# Revit family: PRD_FrankeWS_TwlRls_MEDIUSDoubleTowelRack_MEDX012HP
name_source: partatom
category: Specialty Equipment
revit_build: Autodesk Revit 2018 (Build: 20190510_1515(x64)
units: mm (PartAtom-declared; Revit-internal decimal feet)

## family parameters
Cut with Voids When Loaded = No
Host = Face
OmniClass Number = 23.40.20.21.27
OmniClass Title = Towel Bars
Part Type = Normal
Room Calculation Point = No
Round Connector Dimension = Use Diameter
Shared = No

## types (1)
- MEDX012HP
    AssetType = Fixed
    BIMObjectName = PRD_AR_TowelRails_MEDIUSDoubleTowelRack_MEDX012HP
    Category = Pr_40_20_76_90, Towel rails
    Default Elevation = 1200 mm
    Description = Double towel rack in combination of towel shelf and rail for wall mounting, 304 stainless steel, round covers to conceal the fixing of screws, inclusive stainless steel screws and dowels.
    DurationUnit = year
    Features = stainless steel, surface high polished
    Finish = high polished
    GrossWeight = 1.31 kg
    IfcExportAs = IfcFurnitureType
    IfcExportType = USERDEFINED
    IntegralAccessories = incl. stainless steel screws and dowels
    IsBuiltIn = TRUE
    MainColor = stainless steel
    Manufacturer = KWC Group AG
    ManufacturerName = KWC Group AG
    ManufacturerURL = www.kwc.com
    Material = stainless steel
    MaterialCode = 1.4301
    Model = MEDX012HP
    ModelNumber = 2000106257
    ModelReference = MEDX012HP
    NBSDescription = Towel rails
    NBSReference = 45-35-72/372
    Name = Double Towel Rack MEDX012HP
    NetWeight = 0.79 kg
    NominalDepth = 220 mm  [stored 0.721785 ft]
    NominalHeight = 120 mm  [stored 0.393701 ft]
    NominalWidth = 600 mm  [stored 1.9685 ft]
    ProductInformation = https://pim.kwc.com
    RailMaterial = PRD_AR_StainlessSteel_HighPolished
    Size = 600 x 120 x 220 mm
    Style = Rack
    TypeOfFixing = Screw
    TypeOfMounting = Wall mounting
    URL = www.kwc.com
    Uniclass2015Code = Pr_40_20_76_90
    Uniclass2015Title = Towel rails
    Uniclass2015Version = Products v1.17
    Version = 1
    WarrantyDurationUnit = year

note: [stored X ft] marks values corroborated as IEEE doubles in the binary element streams (Revit-internal decimal feet)

## geometry (parser evidence)
native form markers: Sweep x1
no freeform markers — native parametric forms only
